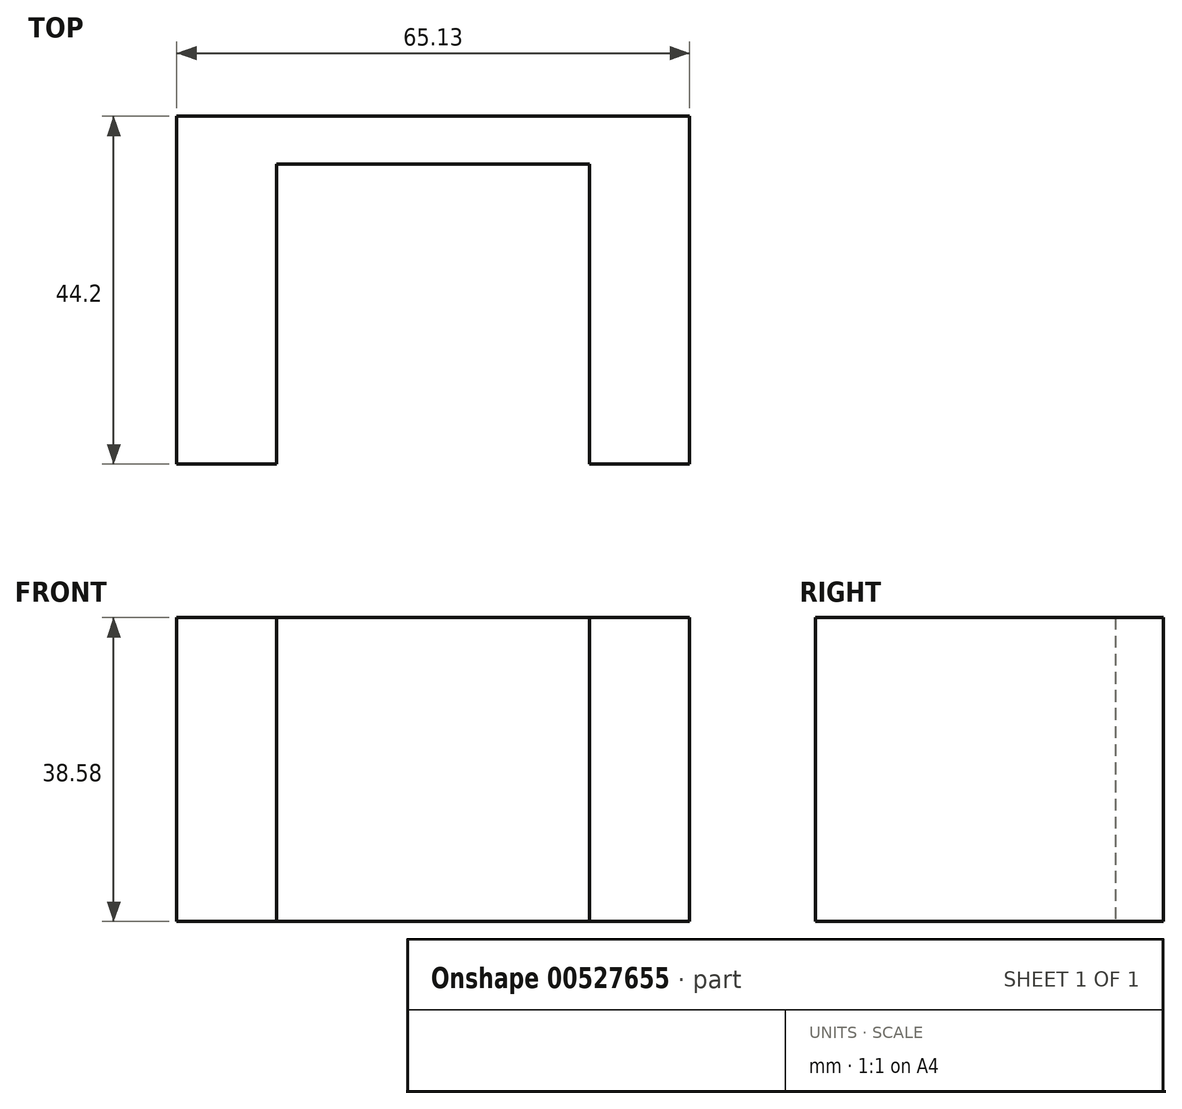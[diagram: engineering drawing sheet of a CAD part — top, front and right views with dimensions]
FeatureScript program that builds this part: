
annotation { "Feature Type Name" : "Feature", "Feature Type Description" : "" }
export const myFeature = defineFeature(function(context is Context, id is Id, definition is map)
    precondition{}
    {
        {
            var Q0;
            Q0=qCreatedBy(makeId("Front.planeOp"),FACE);
            var sketch = newSketch(context, id + "F0", { "sketchPlane" : qUnion([Q0])});
            skLineSegment(sketch, "E0.bottom", {"start": v(-71.82, 71.04) * mm, "end": v(-6.69, 71.04) * mm});
            skLineSegment(sketch, "E0.top", {"start": v(-71.82, 32.46) * mm, "end": v(-6.69, 32.46) * mm});
            skLineSegment(sketch, "E0.left", {"start": v(-71.82, 71.04) * mm, "end": v(-71.82, 32.46) * mm});
            skLineSegment(sketch, "E0.right", {"start": v(-6.69, 71.04) * mm, "end": v(-6.69, 32.46) * mm});
            skSolve(sketch);
        }
        {
            var Q0;
            Q0=makeQuery(id+"F0.imprint","IMPRINT",FACE,{"disambiguationData":[TD([[makeQuery(id+"F0.imprint","IMPRINT",EDGE,{"derivedFrom":sQuery(id+"F0.wireOp",EDGE,"E0.bottom")}),-1.0]])]});
            extrude(context, id + "F1", {"entities" : qUnion([Q0]), "depth" : 6.1 * mm, "offsetDistance" : 25.4 * mm});
        }
        {
            var Q0;
            Q0=makeQuery(id+"F1.opExtrude","CAP_FACE",FACE,{"disambiguationData":[OSD([sQuery(id+"F0.wireOp",EDGE,"E0.bottom"),sQuery(id+"F0.wireOp",EDGE,"E0.top"),sQuery(id+"F0.wireOp",EDGE,"E0.left"),sQuery(id+"F0.wireOp",EDGE,"E0.right")])],"isStart":false});
            var sketch = newSketch(context, id + "F2", { "sketchPlane" : qUnion([Q0])});
            skLineSegment(sketch, "E1.bottom", {"start": v(-59.12, 71.04) * mm, "end": v(-71.82, 71.04) * mm});
            skLineSegment(sketch, "E1.top", {"start": v(-59.12, 32.46) * mm, "end": v(-71.82, 32.46) * mm});
            skLineSegment(sketch, "E1.left", {"start": v(-59.12, 71.04) * mm, "end": v(-59.12, 32.46) * mm});
            skLineSegment(sketch, "E1.right", {"start": v(-71.82, 71.04) * mm, "end": v(-71.82, 32.46) * mm});
            skLineSegment(sketch, "E2.bottom", {"start": v(-19.39, 71.04) * mm, "end": v(-6.69, 71.04) * mm});
            skLineSegment(sketch, "E2.top", {"start": v(-19.39, 32.46) * mm, "end": v(-6.69, 32.46) * mm});
            skLineSegment(sketch, "E2.left", {"start": v(-19.39, 71.04) * mm, "end": v(-19.39, 32.46) * mm});
            skLineSegment(sketch, "E2.right", {"start": v(-6.69, 71.04) * mm, "end": v(-6.69, 32.46) * mm});
            skSolve(sketch);
        }
        {
            var Q0;
            Q0=makeQuery(id+"F2.imprint","IMPRINT",FACE,{"disambiguationData":[TD([[makeQuery(id+"F2.imprint","IMPRINT",EDGE,{"derivedFrom":sQuery(id+"F2.wireOp",EDGE,"E1.bottom")}),-1.0]])]});
            var Q1;
            Q1=makeQuery(id+"F2.imprint","IMPRINT",FACE,{"disambiguationData":[TD([[makeQuery(id+"F2.imprint","IMPRINT",EDGE,{"derivedFrom":sQuery(id+"F2.wireOp",EDGE,"E2.bottom")}),-1.0]])]});
            extrude(context, id + "F3", {"entities" : qUnion([Q0, Q1]), "operationType" : NewBodyOperationType.ADD, "depth" : 38.1 * mm, "offsetDistance" : 25.4 * mm});
        }
    });
